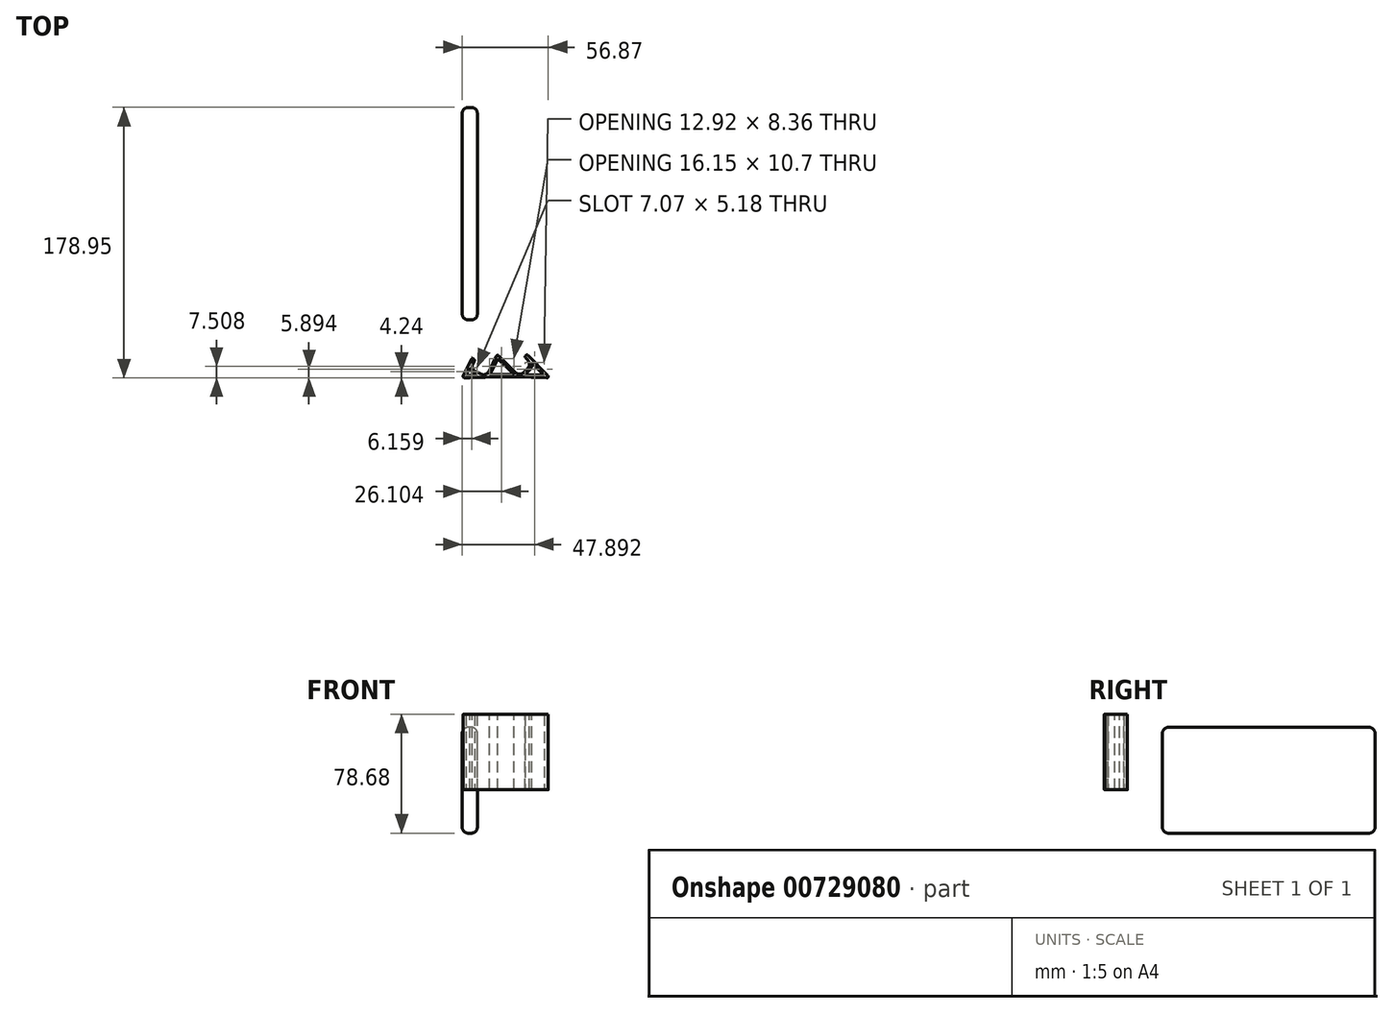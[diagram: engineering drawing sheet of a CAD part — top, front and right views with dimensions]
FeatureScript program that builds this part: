
annotation { "Feature Type Name" : "Feature", "Feature Type Description" : "" }
export const myFeature = defineFeature(function(context is Context, id is Id, definition is map)
    precondition{}
    {
        {
            var Q0;
            Q0=qCreatedBy(makeId("Right.planeOp"),FACE);
            var sketch = newSketch(context, id + "F0", { "sketchPlane" : qUnion([Q0])});
            skLineSegment(sketch, "E0.bottom", {"start": v(38.43, -28.68) * mm, "end": v(179.03, -28.68) * mm});
            skLineSegment(sketch, "E0.top", {"start": v(38.43, 41.32) * mm, "end": v(179.03, 41.32) * mm});
            skLineSegment(sketch, "E0.left", {"start": v(38.43, -28.68) * mm, "end": v(38.43, 41.32) * mm});
            skLineSegment(sketch, "E0.right", {"start": v(179.03, -28.68) * mm, "end": v(179.03, 41.32) * mm});
            skSolve(sketch);
        }
        {
            var Q0;
            Q0 = qSketchRegion(id + "F0", true);
            extrude(context, id + "F1", {"entities" : qUnion([Q0]), "depth" : 10 * mm, "offsetDistance" : 25 * mm});
        }
        {
            var Q0;
            Q0=makeQuery(id+"F1.opExtrude","CAP_FACE",FACE,{"disambiguationData":[OSD([sQuery(id+"F0.wireOp",EDGE,"E0.bottom"),sQuery(id+"F0.wireOp",EDGE,"E0.top"),sQuery(id+"F0.wireOp",EDGE,"E0.left"),sQuery(id+"F0.wireOp",EDGE,"E0.right")])],"isStart":true});
            var Q1;
            Q1=makeQuery(id+"F1.opExtrude","CAP_FACE",FACE,{"disambiguationData":[OSD([sQuery(id+"F0.wireOp",EDGE,"E0.bottom"),sQuery(id+"F0.wireOp",EDGE,"E0.top"),sQuery(id+"F0.wireOp",EDGE,"E0.left"),sQuery(id+"F0.wireOp",EDGE,"E0.right")])],"isStart":false});
            var Q2;
            Q2=makeQuery(id+"F1.opExtrude","SWEPT_EDGE",EDGE,{"disambiguationData":[OSD([sQuery(id+"F0.wireOp",EDGE,"E0.top"),sQuery(id+"F0.wireOp",EDGE,"E0.left")])]});
            var Q3;
            Q3=makeQuery(id+"F1.opExtrude","SWEPT_EDGE",EDGE,{"disambiguationData":[OSD([sQuery(id+"F0.wireOp",EDGE,"E0.bottom"),sQuery(id+"F0.wireOp",EDGE,"E0.left")])]});
            var Q4;
            Q4=makeQuery(id+"F1.opExtrude","SWEPT_EDGE",EDGE,{"disambiguationData":[OSD([sQuery(id+"F0.wireOp",EDGE,"E0.bottom"),sQuery(id+"F0.wireOp",EDGE,"E0.right")])]});
            var Q5;
            Q5=makeQuery(id+"F1.opExtrude","SWEPT_EDGE",EDGE,{"disambiguationData":[OSD([sQuery(id+"F0.wireOp",EDGE,"E0.top"),sQuery(id+"F0.wireOp",EDGE,"E0.right")])]});
            fillet(context, id + "F2", {"entities" : qUnion([Q0, Q1, Q2, Q3, Q4, Q5]), "radius" : 4 * mm, "tangentPropagation" : true, "allowEdgeOverflow" : false});
        }
        {
            var Q0;
            Q0=qCreatedBy(makeId("Top.planeOp"),FACE);
            var sketch = newSketch(context, id + "F3", { "sketchPlane" : qUnion([Q0])});
            skLineSegment(sketch, "E1", {"start": v(58.41, 0) * mm, "end": v(42.75, 15.66) * mm});
            skLineSegment(sketch, "E2", {"start": v(42.75, 15.66) * mm, "end": v(41.2, 14.1) * mm});
            skLineSegment(sketch, "E3", {"start": v(41.2, 14.1) * mm, "end": v(46.14, 9.16) * mm});
            skLineSegment(sketch, "E4", {"start": v(46.14, 9.16) * mm, "end": v(37.87, 0.88) * mm});
            skLineSegment(sketch, "E5", {"start": v(37.87, 0.88) * mm, "end": v(23.1, 15.65) * mm});
            skLineSegment(sketch, "E6", {"start": v(23.1, 15.65) * mm, "end": v(15.85, 0.8) * mm});
            skLineSegment(sketch, "E7", {"start": v(15.85, 0.8) * mm, "end": v(5.34, 5.92) * mm});
            skLineSegment(sketch, "E8", {"start": v(5.34, 5.92) * mm, "end": v(8.4, 12.21) * mm});
            skLineSegment(sketch, "E9", {"start": v(8.4, 12.21) * mm, "end": v(6.43, 13.18) * mm});
            skLineSegment(sketch, "E10", {"start": v(6.43, 13.18) * mm, "end": v(0, 0) * mm});
            skLineSegment(sketch, "E11", {"start": v(23.1, 15.65) * mm, "end": v(23.1, 0) * mm, "construction": true});
            skLineSegment(sketch, "E12", {"start": v(15.85, 0.8) * mm, "end": v(77.49, 127.16) * mm, "construction": true});
            skLineSegment(sketch, "E13", {"start": v(15.85, 0.8) * mm, "end": v(5.34, 5.92) * mm, "construction": true});
            skLineSegment(sketch, "E14", {"start": v(5.34, 5.92) * mm, "end": v(66.97, 132.3) * mm, "construction": true});
            skLineSegment(sketch, "E15", {"start": v(66.97, 132.3) * mm, "end": v(77.49, 127.16) * mm, "construction": true});
            skLineSegment(sketch, "E16", {"start": v(37.87, 0.88) * mm, "end": v(-11.63, 50.38) * mm, "construction": true});
            skLineSegment(sketch, "E17", {"start": v(37.87, 0.88) * mm, "end": v(46.14, 9.16) * mm, "construction": true});
            skLineSegment(sketch, "E18", {"start": v(46.14, 9.16) * mm, "end": v(-3.35, 58.65) * mm, "construction": true});
            skLineSegment(sketch, "E19", {"start": v(-3.35, 58.65) * mm, "end": v(-11.63, 50.38) * mm, "construction": true});
            skLineSegment(sketch, "E20", {"start": v(58.41, 0) * mm, "end": v(58.41, 88.05) * mm, "construction": true});
            skPoint(sketch, "E20.endSnap0", {"position": v(72.23, 129.73) * mm});
            skLineSegment(sketch, "E21", {"start": v(36.15, 69.1) * mm, "end": v(46.67, 63.98) * mm, "construction": true});
            skLineSegment(sketch, "E22", {"start": v(41.41, 66.54) * mm, "end": v(41.41, 0) * mm, "construction": true});
            skArc(sketch, "E23", {"start": v(58.41, 0) * mm, "mid": v(29.2, 0.75) * mm, "end": v(0, 0) * mm});
            skLineSegment(sketch, "E24", {"start": v(0, 0) * mm, "end": v(58.41, 0) * mm, "construction": true});
            skLineSegment(sketch, "E25", {"start": v(17.26, 0) * mm, "end": v(17.26, 29.77) * mm, "construction": true});
            skPoint(sketch, "E26", {"position": v(17.26, 29.77) * mm});
            skLineSegment(sketch, "E27", {"start": v(58.41, 0) * mm, "end": v(41.41, 66.54) * mm, "construction": true});
            skLineSegment(sketch, "E28", {"start": v(21.4, 33.9) * mm, "end": v(13.12, 25.63) * mm, "construction": true});
            skSolve(sketch);
        }
        {
            var Q0;
            {var subQ5=sQuery(id+"F3.wireOp",EDGE,"E2");Q0=makeQuery(id+"F3.imprint","IMPRINT",FACE,{"disambiguationData":[TD([[makeQuery(id+"F3.imprint","IMPRINT",EDGE,{"derivedFrom":subQ5}),1.0]])]});}
            var Q1;
            {var subQ0=sQuery(id+"F3.wireOp",EDGE,"E1");var subQ1=sQuery(id+"F3.wireOp",EDGE,"3Ye0FZxl-FkT7-tVTo-dLDi-VFVJxXrmrOT7");var subQ2=makeQuery(id+"F3.imprint","INTERSECT",VERTEX,{"derivedFrom":[subQ1,subQ0]});Q1=makeQuery(id+"F3.imprint","IMPRINT",FACE,{"disambiguationData":[TD([[makeQuery(id+"F3.imprint","IMPRINT",EDGE,{"disambiguationData":[TD([[subQ2,1.0]])],"derivedFrom":subQ1}),-1.0]])]});}
            var Q2;
            {var subQ0=sQuery(id+"F3.wireOp",EDGE,"E10");var subQ1=sQuery(id+"F3.wireOp",EDGE,"3Ye0FZxl-FkT7-tVTo-dLDi-VFVJxXrmrOT7");var subQ2=makeQuery(id+"F3.imprint","INTERSECT",VERTEX,{"derivedFrom":[subQ1,subQ0]});Q2=makeQuery(id+"F3.imprint","IMPRINT",FACE,{"disambiguationData":[TD([[makeQuery(id+"F3.imprint","IMPRINT",EDGE,{"disambiguationData":[TD([[subQ2,-1.0]])],"derivedFrom":subQ1}),-1.0]])]});}
            extrude(context, id + "F4", {"entities" : qUnion([Q0, Q1, Q2]), "depth" : 50 * mm, "offsetDistance" : 25 * mm});
        }
        {
            var Q0;
            Q0=makeQuery(id+"F4.opExtrude","SWEPT_EDGE",EDGE,{"disambiguationData":[OSD([sQuery(id+"F3.wireOp",EDGE,"E6"),sQuery(id+"F3.wireOp",EDGE,"E7")])]});
            var Q1;
            Q1=makeQuery(id+"F4.opExtrude","SWEPT_EDGE",EDGE,{"disambiguationData":[OSD([sQuery(id+"F3.wireOp",EDGE,"E4"),sQuery(id+"F3.wireOp",EDGE,"E5")])]});
            var Q2;
            Q2=makeQuery(id+"F4.opExtrude","SWEPT_EDGE",EDGE,{"disambiguationData":[OSD([sQuery(id+"F3.wireOp",EDGE,"E3"),sQuery(id+"F3.wireOp",EDGE,"E4")])]});
            var Q3;
            Q3=makeQuery(id+"F4.opExtrude","SWEPT_EDGE",EDGE,{"disambiguationData":[OSD([sQuery(id+"F3.wireOp",EDGE,"E7"),sQuery(id+"F3.wireOp",EDGE,"E8")])]});
            fillet(context, id + "F5", {"entities" : qUnion([Q0, Q1, Q2, Q3]), "radius" : 4 * mm, "tangentPropagation" : true, "allowEdgeOverflow" : false});
        }
        {
            var Q0;
            Q0=makeQuery(id+"F4.opExtrude","SWEPT_EDGE",EDGE,{"disambiguationData":[OSD([sQuery(id+"F3.wireOp",EDGE,"E2"),sQuery(id+"F3.wireOp",EDGE,"E3")])]});
            var Q1;
            Q1=makeQuery(id+"F4.opExtrude","SWEPT_EDGE",EDGE,{"disambiguationData":[OSD([sQuery(id+"F3.wireOp",EDGE,"E8"),sQuery(id+"F3.wireOp",EDGE,"E9")])]});
            var Q2;
            Q2=makeQuery(id+"F4.opExtrude","SWEPT_EDGE",EDGE,{"disambiguationData":[OSD([sQuery(id+"F3.wireOp",EDGE,"E1"),sQuery(id+"F3.wireOp",EDGE,"E2")])]});
            var Q3;
            Q3=makeQuery(id+"F4.opExtrude","SWEPT_EDGE",EDGE,{"disambiguationData":[OSD([sQuery(id+"F3.wireOp",EDGE,"E9"),sQuery(id+"F3.wireOp",EDGE,"E10")])]});
            var Q4;
            Q4=makeQuery(id+"F4.opExtrude","SWEPT_EDGE",EDGE,{"disambiguationData":[OSD([sQuery(id+"F3.wireOp",EDGE,"3Ye0FZxl-FkT7-tVTo-dLDi-VFVJxXrmrOT7"),sQuery(id+"F3.wireOp",EDGE,"E1")])]});
            var Q5;
            Q5=makeQuery(id+"F4.opExtrude","SWEPT_EDGE",EDGE,{"disambiguationData":[OSD([sQuery(id+"F3.wireOp",EDGE,"3Ye0FZxl-FkT7-tVTo-dLDi-VFVJxXrmrOT7"),sQuery(id+"F3.wireOp",EDGE,"E10")])]});
            var Q6;
            Q6=makeQuery(id+"F4.opExtrude","SWEPT_EDGE",EDGE,{"disambiguationData":[OSD([sQuery(id+"F3.wireOp",EDGE,"E5"),sQuery(id+"F3.wireOp",EDGE,"E6")])]});
            fillet(context, id + "F6", {"entities" : qUnion([Q0, Q1, Q2, Q3, Q4, Q5, Q6]), "radius" : 1 * mm, "tangentPropagation" : true, "allowEdgeOverflow" : false});
        }
        {
            var Q0;
            Q0=makeQuery(id+"F4.opExtrude","CAP_FACE",FACE,{"disambiguationData":[OSD([sQuery(id+"F3.wireOp",EDGE,"3Ye0FZxl-FkT7-tVTo-dLDi-VFVJxXrmrOT7"),sQuery(id+"F3.wireOp",EDGE,"E1"),sQuery(id+"F3.wireOp",EDGE,"E2"),sQuery(id+"F3.wireOp",EDGE,"E3"),sQuery(id+"F3.wireOp",EDGE,"E4"),sQuery(id+"F3.wireOp",EDGE,"E5"),sQuery(id+"F3.wireOp",EDGE,"E6"),sQuery(id+"F3.wireOp",EDGE,"E7"),sQuery(id+"F3.wireOp",EDGE,"E8"),sQuery(id+"F3.wireOp",EDGE,"E9"),sQuery(id+"F3.wireOp",EDGE,"E10")])],"isStart":false});
            var Q1;
            Q1=makeQuery(id+"F4.opExtrude","CAP_FACE",FACE,{"disambiguationData":[OSD([sQuery(id+"F3.wireOp",EDGE,"3Ye0FZxl-FkT7-tVTo-dLDi-VFVJxXrmrOT7"),sQuery(id+"F3.wireOp",EDGE,"E1"),sQuery(id+"F3.wireOp",EDGE,"E2"),sQuery(id+"F3.wireOp",EDGE,"E3"),sQuery(id+"F3.wireOp",EDGE,"E4"),sQuery(id+"F3.wireOp",EDGE,"E5"),sQuery(id+"F3.wireOp",EDGE,"E6"),sQuery(id+"F3.wireOp",EDGE,"E7"),sQuery(id+"F3.wireOp",EDGE,"E8"),sQuery(id+"F3.wireOp",EDGE,"E9"),sQuery(id+"F3.wireOp",EDGE,"E10")])],"isStart":true});
            shell(context, id + "F7", {"entities" : qUnion([Q0, Q1]), "thickness" : 1.6 * mm});
        }
    });
